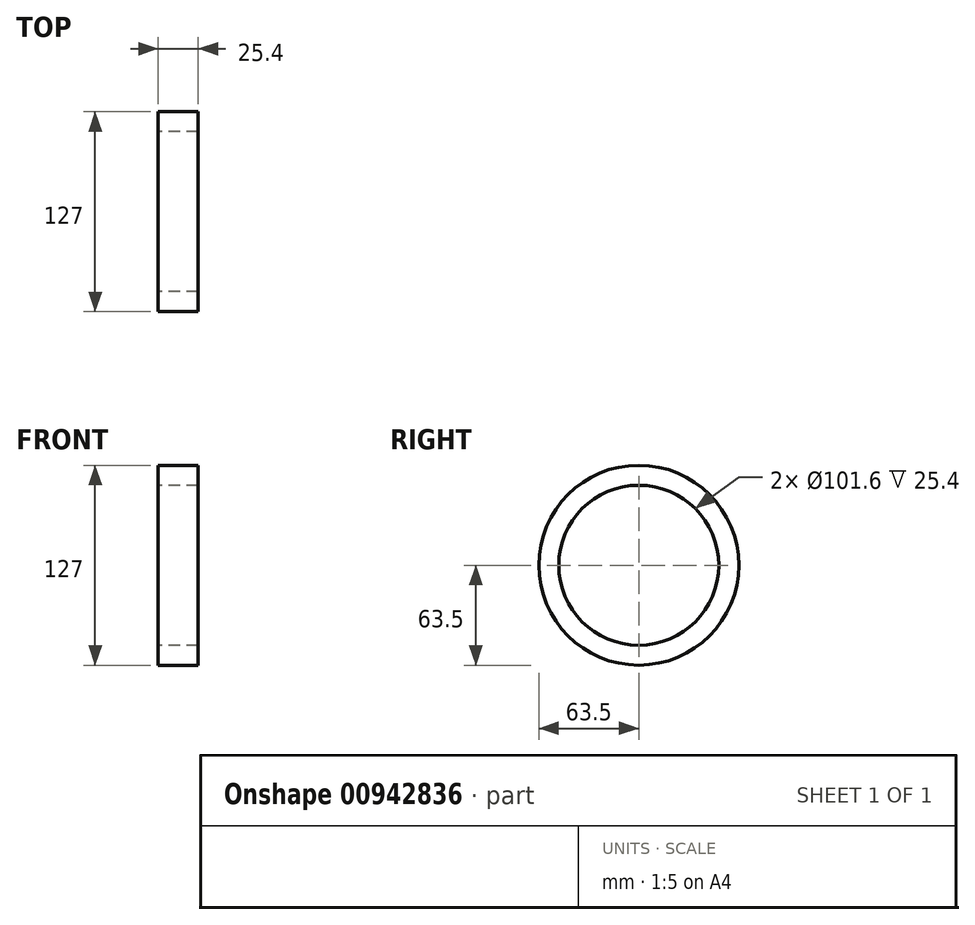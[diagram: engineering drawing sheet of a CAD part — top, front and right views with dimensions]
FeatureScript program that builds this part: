
annotation { "Feature Type Name" : "Feature", "Feature Type Description" : "" }
export const myFeature = defineFeature(function(context is Context, id is Id, definition is map)
    precondition{}
    {
        {
            var Q0;
            Q0=qCreatedBy(makeId("Right.planeOp"),FACE);
            var sketch = newSketch(context, id + "F0", { "sketchPlane" : qUnion([Q0])});
            skCircle(sketch, "E0", {"center": v(0, 0) * mm, "radius": 63.5 * mm});
            skCircle(sketch, "E1", {"center": v(0, 0) * mm, "radius": 50.8 * mm});
            skSolve(sketch);
        }
        {
            var Q0;
            Q0 = qSketchRegion(id + "F0", true);
            extrude(context, id + "F1", {"entities" : qUnion([Q0]), "depth" : 25.4 * mm, "offsetDistance" : 25.4 * mm});
        }
    });
